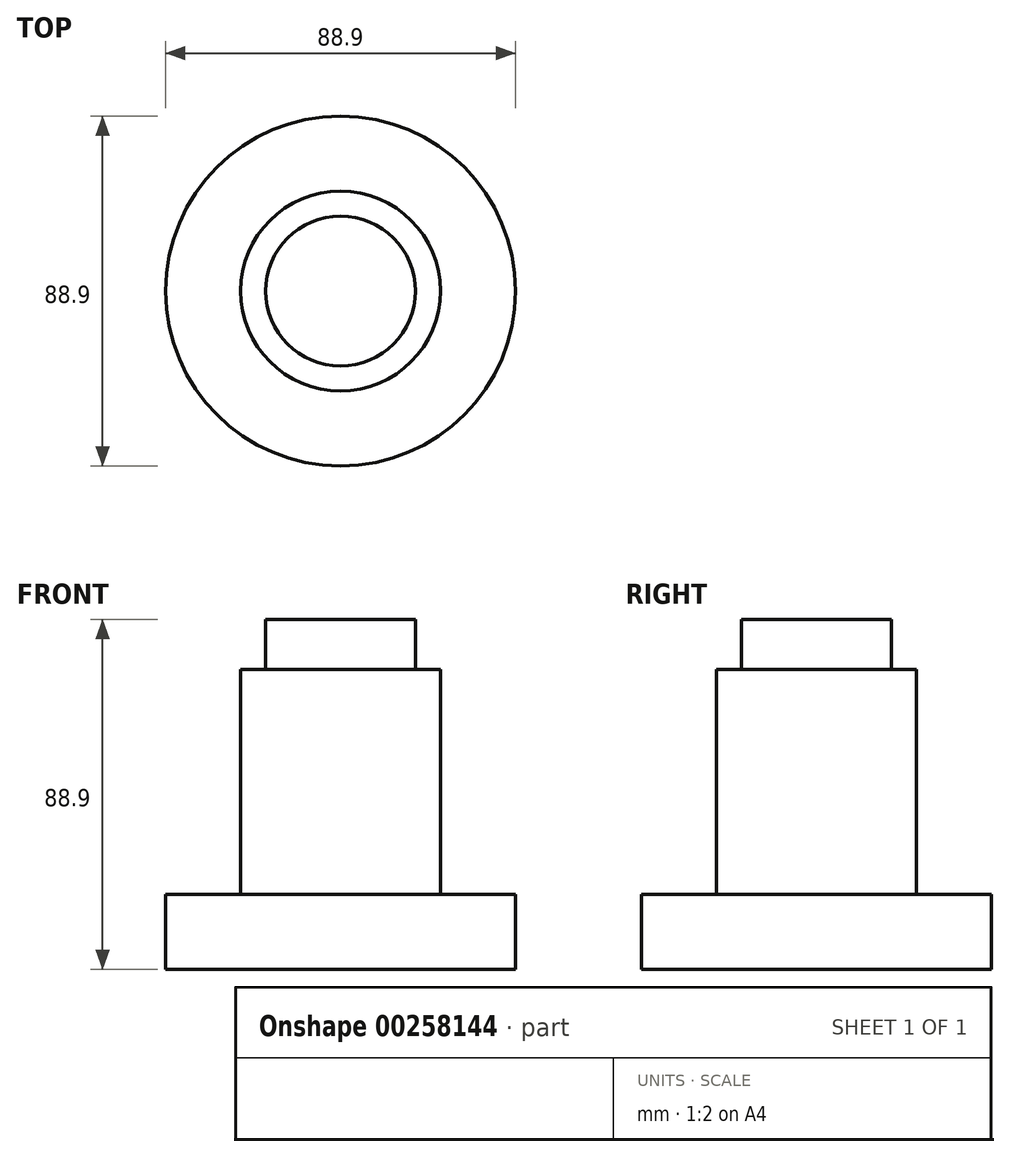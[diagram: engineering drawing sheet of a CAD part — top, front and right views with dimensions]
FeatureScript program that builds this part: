
annotation { "Feature Type Name" : "Feature", "Feature Type Description" : "" }
export const myFeature = defineFeature(function(context is Context, id is Id, definition is map)
    precondition{}
    {
        {
            var Q0;
            Q0=qCreatedBy(makeId("Top.planeOp"),FACE);
            var sketch = newSketch(context, id + "F0", { "sketchPlane" : qUnion([Q0])});
            skCircle(sketch, "E0", {"center": v(0, 0) * mm, "radius": 9.53 * mm});
            skSolve(sketch);
        }
        {
            var Q0;
            Q0=makeQuery(id+"F0.imprint","IMPRINT",FACE,{"disambiguationData":[TD([[makeQuery(id+"F0.imprint","IMPRINT",EDGE,{"derivedFrom":sQuery(id+"F0.wireOp",EDGE,"E0")}),1.0]])]});
            extrude(context, id + "F1", {"entities" : qUnion([Q0]), "depth" : 88.9 * mm});
        }
        {
            var Q0;
            Q0=qCreatedBy(makeId("Front.planeOp"),FACE);
            var sketch = newSketch(context, id + "F2", { "sketchPlane" : qUnion([Q0])});
            skLineSegment(sketch, "E1", {"start": v(0, 0) * mm, "end": v(44.45, 0) * mm});
            skLineSegment(sketch, "E2", {"start": v(0, 0) * mm, "end": v(0, 19.05) * mm});
            skLineSegment(sketch, "E3", {"start": v(0, 19.05) * mm, "end": v(25.4, 19.05) * mm});
            skLineSegment(sketch, "E4", {"start": v(0, 19.05) * mm, "end": v(0, 76.2) * mm});
            skLineSegment(sketch, "E5", {"start": v(0, 76.2) * mm, "end": v(0, 88.9) * mm});
            skLineSegment(sketch, "E6", {"start": v(0, 19.05) * mm, "end": v(44.45, 19.05) * mm});
            skLineSegment(sketch, "E7", {"start": v(0, 88.9) * mm, "end": v(19.05, 88.9) * mm});
            skLineSegment(sketch, "E8", {"start": v(0, 76.2) * mm, "end": v(25.4, 76.2) * mm});
            skLineSegment(sketch, "E9", {"start": v(0, 76.2) * mm, "end": v(19.05, 76.2) * mm});
            skLineSegment(sketch, "E10", {"start": v(19.05, 88.9) * mm, "end": v(19.05, 76.2) * mm});
            skLineSegment(sketch, "E11", {"start": v(25.4, 76.2) * mm, "end": v(25.4, 19.05) * mm});
            skLineSegment(sketch, "E12", {"start": v(44.45, 19.05) * mm, "end": v(44.45, 0) * mm});
            skSolve(sketch);
        }
        {
            var Q0;
            Q0 = qSketchRegion(id + "F2", true);
            var Q1;
            Q1=makeQuery(id+"F1.opExtrude","SWEPT_FACE",FACE,{"disambiguationData":[OSD([sQuery(id+"F0.wireOp",EDGE,"E0")])]});
            revolve(context, id + "F3", {"operationType" : NewBodyOperationType.ADD, "entities" : qUnion([Q0]), "axis" : qUnion([Q1]), "revolveType" : RevolveType.FULL});
        }
    });
